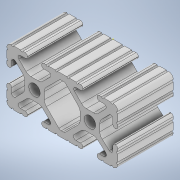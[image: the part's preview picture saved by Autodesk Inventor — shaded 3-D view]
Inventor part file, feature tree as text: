
AUTODESK INVENTOR PART (.ipt)
format: ipt  version: 2020 (Build 240168000, 168)  size: 337,920 bytes
history: native  units: in
note: dims shown in document units (in); Inventor stores cm internally (conversion verified against a paired STEP export)
features: sketch x2, extrude x1
ambient origin geometry x8: Origin, YZ Plane, XZ Plane, XY Plane, X Axis, Y Axis, Z Axis, Center Point
bodies: Solid1 (feature_tree)
feature tree (3):
  extrude  "Extrusion1"  [1 undecoded]
  sketch  "Sketch2"
  sketch  "Sketch1"  dims[d0=1.0in d1=0.0in]
note: 1 required parameter value undecoded (feature->parameter linkage not recoverable at this tier; creation-order binding heuristic only, values carry confidence <= 0.55)
